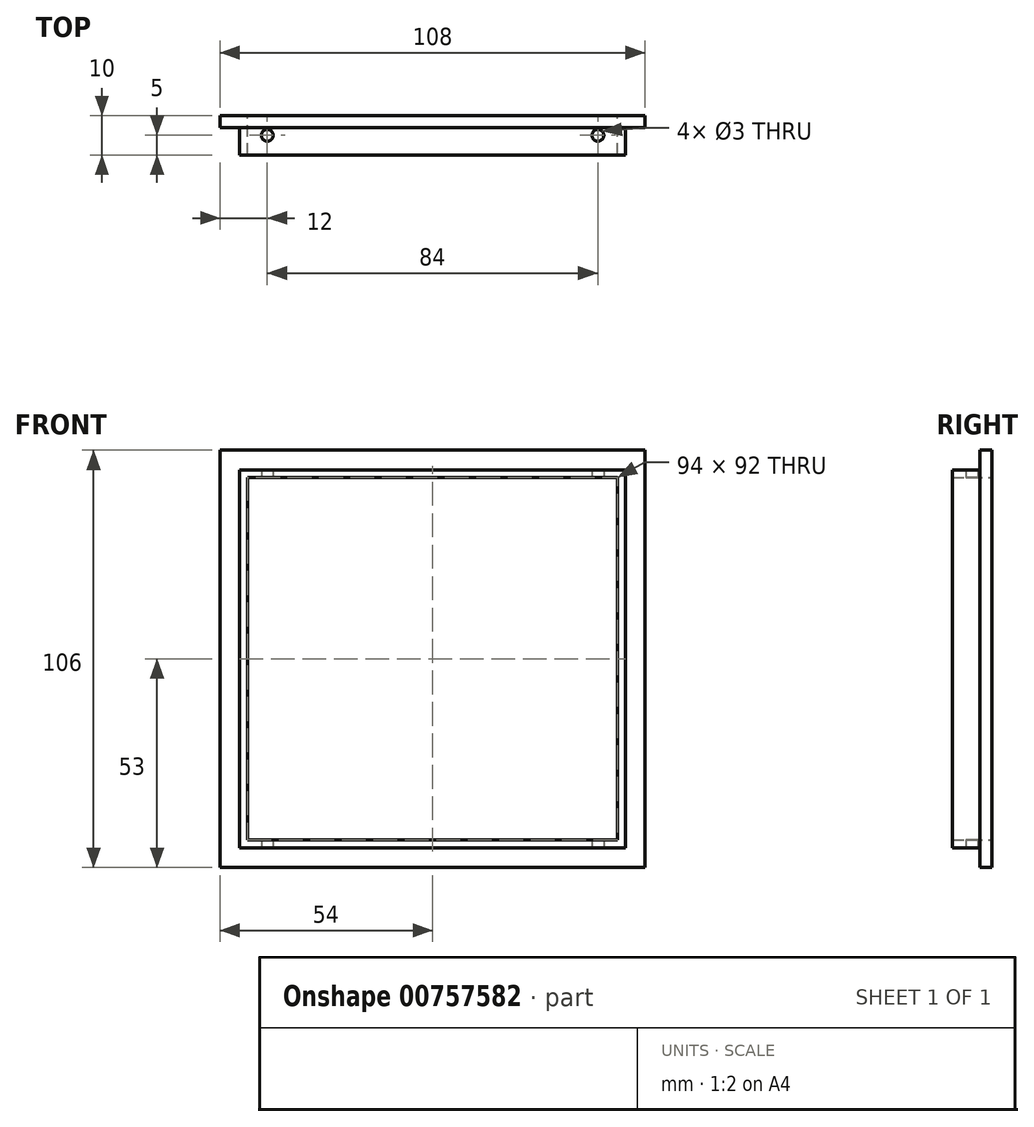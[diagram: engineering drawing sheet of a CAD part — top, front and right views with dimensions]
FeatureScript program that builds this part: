
annotation { "Feature Type Name" : "Feature", "Feature Type Description" : "" }
export const myFeature = defineFeature(function(context is Context, id is Id, definition is map)
    precondition{}
    {
        {
            var Q0;
            Q0=qCreatedBy(makeId("Front.planeOp"),FACE);
            var sketch = newSketch(context, id + "F0", { "sketchPlane" : qUnion([Q0])});
            skLineSegment(sketch, "E0.bottom", {"start": v(0, 0) * mm, "end": v(108, 0) * mm});
            skLineSegment(sketch, "E0.top", {"start": v(0, 106) * mm, "end": v(108, 106) * mm});
            skLineSegment(sketch, "E0.left", {"start": v(0, 0) * mm, "end": v(0, 106) * mm});
            skLineSegment(sketch, "E0.right", {"start": v(108, 0) * mm, "end": v(108, 106) * mm});
            skLineSegment(sketch, "E1.bottom", {"start": v(5, 101) * mm, "end": v(103, 101) * mm});
            skLineSegment(sketch, "E1.top", {"start": v(5, 5) * mm, "end": v(103, 5) * mm});
            skLineSegment(sketch, "E1.left", {"start": v(5, 101) * mm, "end": v(5, 5) * mm});
            skLineSegment(sketch, "E1.right", {"start": v(103, 101) * mm, "end": v(103, 5) * mm});
            skLineSegment(sketch, "E2.bottom", {"start": v(7, 99) * mm, "end": v(101, 99) * mm});
            skLineSegment(sketch, "E2.top", {"start": v(7, 7) * mm, "end": v(101, 7) * mm});
            skLineSegment(sketch, "E2.left", {"start": v(7, 99) * mm, "end": v(7, 7) * mm});
            skLineSegment(sketch, "E2.right", {"start": v(101, 99) * mm, "end": v(101, 7) * mm});
            skSolve(sketch);
        }
        {
            var Q0;
            Q0=makeQuery(id+"F0.imprint","IMPRINT",FACE,{"disambiguationData":[TD([[makeQuery(id+"F0.imprint","IMPRINT",EDGE,{"derivedFrom":sQuery(id+"F0.wireOp",EDGE,"E1.bottom")}),-1.0]])]});
            extrude(context, id + "F1", {"entities" : qUnion([Q0]), "depth" : 10 * mm, "offsetDistance" : 25 * mm});
        }
        {
            var Q0;
            Q0 = qSketchRegion(id + "F0", true);
            extrude(context, id + "F2", {"entities" : qUnion([Q0]), "operationType" : NewBodyOperationType.ADD, "depth" : 3 * mm, "offsetDistance" : 25 * mm});
        }
        {
            var Q0;
            Q0=qCreatedBy(makeId("Top.planeOp"),FACE);
            var sketch = newSketch(context, id + "F3", { "sketchPlane" : qUnion([Q0])});
            skPoint(sketch, "E3", {"position": v(96, -5) * mm});
            skPoint(sketch, "E4", {"position": v(12, -5) * mm});
            skSolve(sketch);
        }
        {
            var Q0;
            Q0=sQuery(id+"F3.wireOp",VERTEX,"E4");
            var Q1;
            Q1=sQuery(id+"F3.wireOp",VERTEX,"E3");
            var Q2;
            Q2=makeQuery(id+"F1.opExtrude","SWEPT_BODY",BODY,{"disambiguationData":[OSD([sQuery(id+"F0.wireOp",EDGE,"E1.bottom"),sQuery(id+"F0.wireOp",EDGE,"E1.top"),sQuery(id+"F0.wireOp",EDGE,"E1.left"),sQuery(id+"F0.wireOp",EDGE,"E1.right"),sQuery(id+"F0.wireOp",EDGE,"E2.bottom"),sQuery(id+"F0.wireOp",EDGE,"E2.top"),sQuery(id+"F0.wireOp",EDGE,"E2.left"),sQuery(id+"F0.wireOp",EDGE,"E2.right")])]});
            hole(context, id + "F4", {"style" : HoleStyle.SIMPLE, "endStyle" : HoleEndStyle.BLIND, "oppositeDirection" : true, "holeDiameter" : 3 * mm, "majorDiameter" : 5 * mm, "holeDepth" : 110 * mm, "isTappedThrough" : true, "tappedDepth" : 12 * mm, "tapClearance" : 3, "locations" : qUnion([Q0, Q1]), "scope" : qUnion([Q2])});
        }
    });
